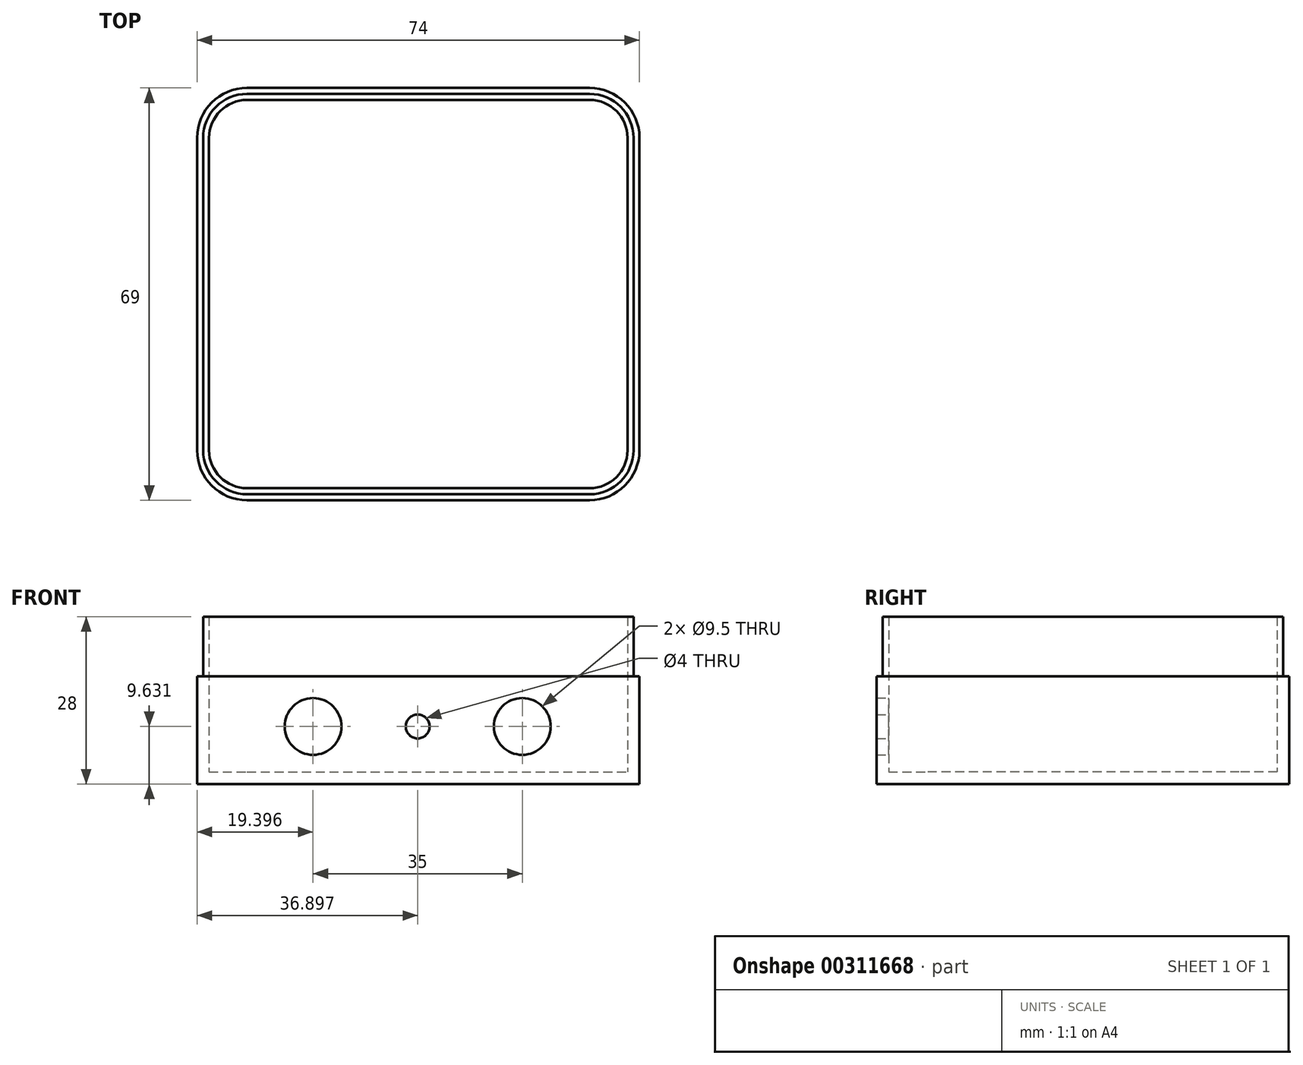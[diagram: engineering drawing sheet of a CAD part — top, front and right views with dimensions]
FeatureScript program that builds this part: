
annotation { "Feature Type Name" : "Feature", "Feature Type Description" : "" }
export const myFeature = defineFeature(function(context is Context, id is Id, definition is map)
    precondition{}
    {
        {
            var Q0;
            Q0=qCreatedBy(makeId("Top.planeOp"),FACE);
            var sketch = newSketch(context, id + "F0", { "sketchPlane" : qUnion([Q0])});
            skLineSegment(sketch, "E0", {"start": v(0, 0) * mm, "end": v(28.65, 0) * mm});
            skLineSegment(sketch, "E1", {"start": v(35, 6.35) * mm, "end": v(35, 58.65) * mm});
            skLineSegment(sketch, "E2", {"start": v(28.65, 65) * mm, "end": v(-28.65, 65) * mm});
            skLineSegment(sketch, "E3", {"start": v(-35, 58.65) * mm, "end": v(-35, 6.35) * mm});
            skLineSegment(sketch, "E4", {"start": v(-28.65, 0) * mm, "end": v(0, 0) * mm});
            skLineSegment(sketch, "E5", {"start": v(0, 0) * mm, "end": v(0, 65) * mm, "construction": true});
            skLineSegment(sketch, "E6", {"start": v(-35, 32.5) * mm, "end": v(35, 32.5) * mm, "construction": true});
            skPoint(sketch, "E7.visualSharp", {"position": v(-35, 0) * mm});
            skArc(sketch, "E7.filletArc", {"start": v(-35, 6.35) * mm, "mid": v(-33.14, 1.86) * mm, "end": v(-28.65, 0) * mm});
            skPoint(sketch, "E8.visualSharp", {"position": v(35, 0) * mm});
            skArc(sketch, "E8.filletArc", {"start": v(28.65, 0) * mm, "mid": v(33.14, 1.86) * mm, "end": v(35, 6.35) * mm});
            skPoint(sketch, "E9.visualSharp", {"position": v(35, 65) * mm});
            skArc(sketch, "E9.filletArc", {"start": v(35, 58.65) * mm, "mid": v(33.14, 63.14) * mm, "end": v(28.65, 65) * mm});
            skPoint(sketch, "E10.visualSharp", {"position": v(-35, 65) * mm});
            skArc(sketch, "E10.filletArc", {"start": v(-28.65, 65) * mm, "mid": v(-33.14, 63.14) * mm, "end": v(-35, 58.65) * mm});
            skArc(sketch, "E11.0", {"start": v(37, 58.65) * mm, "mid": v(34.55, 64.55) * mm, "end": v(28.65, 67) * mm});
            skLineSegment(sketch, "E11.1", {"start": v(37, 6.35) * mm, "end": v(37, 58.65) * mm});
            skLineSegment(sketch, "E11.2", {"start": v(28.65, 67) * mm, "end": v(-28.65, 67) * mm});
            skArc(sketch, "E11.3", {"start": v(28.65, -2) * mm, "mid": v(34.55, 0.45) * mm, "end": v(37, 6.35) * mm});
            skLineSegment(sketch, "E11.4", {"start": v(0, -2) * mm, "end": v(28.65, -2) * mm});
            skArc(sketch, "E11.5", {"start": v(-28.65, 67) * mm, "mid": v(-34.55, 64.55) * mm, "end": v(-37, 58.65) * mm});
            skLineSegment(sketch, "E11.6", {"start": v(-37, 58.65) * mm, "end": v(-37, 6.35) * mm});
            skArc(sketch, "E11.7", {"start": v(-37, 6.35) * mm, "mid": v(-34.55, 0.45) * mm, "end": v(-28.65, -2) * mm});
            skLineSegment(sketch, "E11.8", {"start": v(-28.65, -2) * mm, "end": v(0, -2) * mm});
            skLineSegment(sketch, "E12", {"start": v(0, 32.5) * mm, "end": v(17.5, 32.5) * mm});
            skLineSegment(sketch, "E13", {"start": v(0, 32.5) * mm, "end": v(-17.5, 32.5) * mm});
            skSolve(sketch);
        }
        {
            var Q0;
            Q0=makeQuery(id+"F0.imprint","IMPRINT",FACE,{"disambiguationData":[TD([[makeQuery(id+"F0.imprint","IMPRINT",EDGE,{"derivedFrom":sQuery(id+"F0.wireOp",EDGE,"E0")}),1.0]])]});
            var Q1;
            Q1=makeQuery(id+"F0.imprint","IMPRINT",FACE,{"disambiguationData":[TD([[makeQuery(id+"F0.imprint","IMPRINT",EDGE,{"derivedFrom":sQuery(id+"F0.wireOp",EDGE,"E0")}),-1.0]])]});
            extrude(context, id + "F1", {"entities" : qUnion([Q0, Q1]), "oppositeDirection" : true, "depth" : 2 * mm});
        }
        {
            var Q0;
            Q0 = qSketchRegion(id + "F0", true);
            extrude(context, id + "F2", {"entities" : qUnion([Q0]), "operationType" : NewBodyOperationType.ADD, "depth" : 26 * mm});
        }
        {
            var Q0;
            Q0=qCreatedBy(makeId("Top.planeOp"),FACE);
            cPlane(context, id + "F3", {"entities" : qUnion([Q0]), "cplaneType" : CPlaneType.OFFSET, "offset" : 26 * mm, "width" : 152.4 * mm, "height" : 152.4 * mm});
        }
        {
            var Q0;
            Q0 = qSketchRegion(id + "F0", true);
            extrude(context, id + "F4", {"entities" : qUnion([Q0]), "operationType" : NewBodyOperationType.ADD, "depth" : 25.4 * mm});
        }
        {
            var Q0;
            Q0=qCreatedBy(id+"F3.planeOp",FACE);
            var sketch = newSketch(context, id + "F5", { "sketchPlane" : qUnion([Q0])});
            skArc(sketch, "E14.0", {"start": v(36, 58.65) * mm, "mid": v(33.85, 63.85) * mm, "end": v(28.65, 66) * mm});
            skLineSegment(sketch, "E14.1", {"start": v(36, 6.35) * mm, "end": v(36, 58.65) * mm});
            skLineSegment(sketch, "E14.2", {"start": v(28.65, 66) * mm, "end": v(-28.65, 66) * mm});
            skArc(sketch, "E14.3", {"start": v(28.65, -1) * mm, "mid": v(33.85, 1.15) * mm, "end": v(36, 6.35) * mm});
            skLineSegment(sketch, "E14.4", {"start": v(0, -1) * mm, "end": v(28.65, -1) * mm});
            skArc(sketch, "E14.5", {"start": v(-28.65, 66) * mm, "mid": v(-33.85, 63.85) * mm, "end": v(-36, 58.65) * mm});
            skLineSegment(sketch, "E14.6", {"start": v(-36, 58.65) * mm, "end": v(-36, 6.35) * mm});
            skArc(sketch, "E14.7", {"start": v(-36, 6.35) * mm, "mid": v(-33.85, 1.15) * mm, "end": v(-28.65, -1) * mm});
            skLineSegment(sketch, "E14.8", {"start": v(-28.65, -1) * mm, "end": v(0, -1) * mm});
            skArc(sketch, "E15.0", {"start": v(37, 58.65) * mm, "mid": v(34.55, 64.55) * mm, "end": v(28.65, 67) * mm});
            skLineSegment(sketch, "E15.1", {"start": v(37, 6.35) * mm, "end": v(37, 58.65) * mm});
            skLineSegment(sketch, "E15.2", {"start": v(28.65, 67) * mm, "end": v(-28.65, 67) * mm});
            skArc(sketch, "E15.3", {"start": v(28.65, -2) * mm, "mid": v(34.55, 0.45) * mm, "end": v(37, 6.35) * mm});
            skLineSegment(sketch, "E15.4", {"start": v(0, -2) * mm, "end": v(28.65, -2) * mm});
            skArc(sketch, "E15.5", {"start": v(-28.65, 67) * mm, "mid": v(-34.55, 64.55) * mm, "end": v(-37, 58.65) * mm});
            skLineSegment(sketch, "E15.6", {"start": v(-37, 58.65) * mm, "end": v(-37, 6.35) * mm});
            skArc(sketch, "E15.7", {"start": v(-37, 6.35) * mm, "mid": v(-34.55, 0.45) * mm, "end": v(-28.65, -2) * mm});
            skLineSegment(sketch, "E15.8", {"start": v(-28.65, -2) * mm, "end": v(0, -2) * mm});
            skSolve(sketch);
        }
        {
            var Q0;
            Q0 = qSketchRegion(id + "F5", true);
            extrude(context, id + "F6", {"entities" : qUnion([Q0]), "operationType" : NewBodyOperationType.REMOVE, "oppositeDirection" : true, "depth" : 10 * mm});
        }
        {
            var Q0;
            Q0=qCreatedBy(makeId("Front.planeOp"),FACE);
            var sketch = newSketch(context, id + "F7", { "sketchPlane" : qUnion([Q0])});
            skLineSegment(sketch, "E16", {"start": v(-32.45, 7.63) * mm, "end": v(32.24, 7.63) * mm, "construction": true});
            skLineSegment(sketch, "E17", {"start": v(-0.1, 7.63) * mm, "end": v(-17.6, 7.63) * mm});
            skLineSegment(sketch, "E18", {"start": v(-0.1, 7.63) * mm, "end": v(17.4, 7.63) * mm});
            skLineSegment(sketch, "E19", {"start": v(17.4, 7.63) * mm, "end": v(22.4, 7.63) * mm});
            skLineSegment(sketch, "E20", {"start": v(-17.6, 7.63) * mm, "end": v(-21.02, 7.63) * mm});
            skCircle(sketch, "E21", {"center": v(-0.1, 7.63) * mm, "radius": 2 * mm});
            skCircle(sketch, "E22", {"center": v(17.4, 7.63) * mm, "radius": 4.75 * mm});
            skCircle(sketch, "E23", {"center": v(-17.6, 7.63) * mm, "radius": 4.75 * mm});
            skSolve(sketch);
        }
        {
            var Q0;
            Q0 = qSketchRegion(id + "F7", true);
            extrude(context, id + "F8", {"entities" : qUnion([Q0]), "operationType" : NewBodyOperationType.REMOVE, "depth" : 25.4 * mm});
        }
    });
